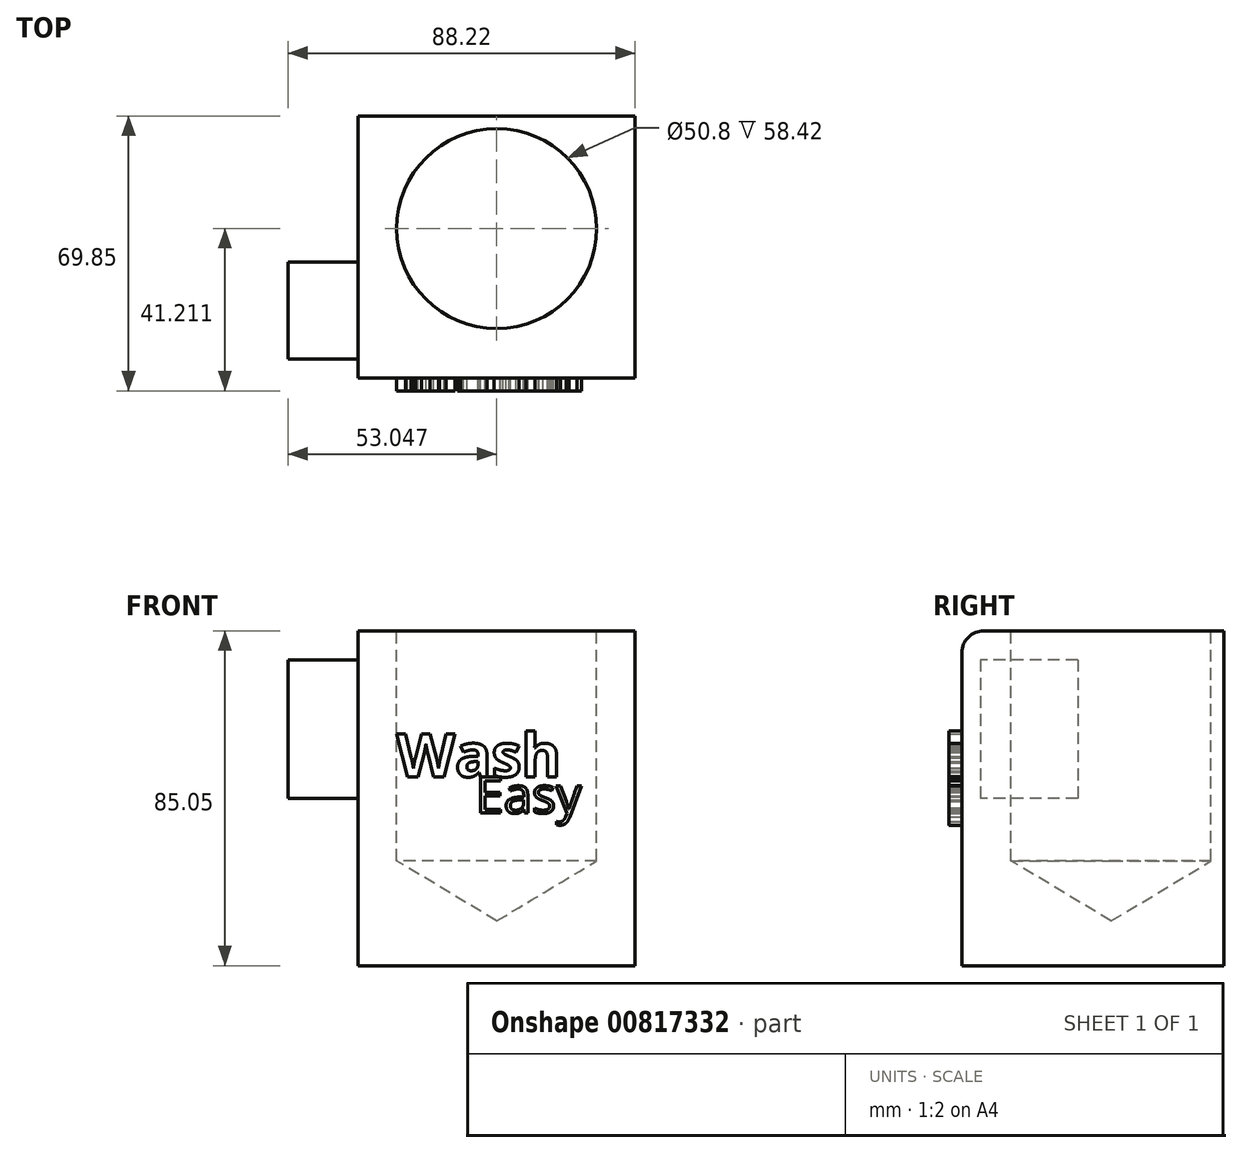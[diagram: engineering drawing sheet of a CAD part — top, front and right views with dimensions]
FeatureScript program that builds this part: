
annotation { "Feature Type Name" : "Feature", "Feature Type Description" : "" }
export const myFeature = defineFeature(function(context is Context, id is Id, definition is map)
    precondition{}
    {
        {
            var Q0;
            Q0=qCreatedBy(makeId("Front.planeOp"),FACE);
            var sketch = newSketch(context, id + "F0", { "sketchPlane" : qUnion([Q0])});
            skLineSegment(sketch, "E0.bottom", {"start": v(-26.72, 37.06) * mm, "end": v(43.72, 37.06) * mm});
            skLineSegment(sketch, "E0.top", {"start": v(-26.72, -47.99) * mm, "end": v(43.72, -47.99) * mm});
            skLineSegment(sketch, "E0.left", {"start": v(-26.72, 37.06) * mm, "end": v(-26.72, -47.99) * mm});
            skLineSegment(sketch, "E0.right", {"start": v(43.72, 37.06) * mm, "end": v(43.72, -47.99) * mm});
            skSolve(sketch);
        }
        {
            var Q0;
            Q0 = qSketchRegion(id + "F0", true);
            extrude(context, id + "F1", {"entities" : qUnion([Q0]), "depth" : 66.55 * mm, "offsetDistance" : 25.4 * mm});
        }
        {
            var Q0;
            Q0=makeQuery(id+"F1.opExtrude","SWEPT_FACE",FACE,{"disambiguationData":[OSD([sQuery(id+"F0.wireOp",EDGE,"E0.left")])]});
            var sketch = newSketch(context, id + "F2", { "sketchPlane" : qUnion([Q0])});
            skLineSegment(sketch, "E1.bottom", {"start": v(37.13, 29.71) * mm, "end": v(61.8, 29.71) * mm});
            skLineSegment(sketch, "E1.top", {"start": v(37.13, -5.46) * mm, "end": v(61.8, -5.46) * mm});
            skLineSegment(sketch, "E1.left", {"start": v(37.13, 29.71) * mm, "end": v(37.13, -5.46) * mm});
            skLineSegment(sketch, "E1.right", {"start": v(61.8, 29.71) * mm, "end": v(61.8, -5.46) * mm});
            skSolve(sketch);
        }
        {
            var Q0;
            Q0 = qSketchRegion(id + "F2", true);
            extrude(context, id + "F3", {"entities" : qUnion([Q0]), "operationType" : NewBodyOperationType.ADD, "depth" : 17.78 * mm, "offsetDistance" : 25.4 * mm});
        }
        {
            var Q0;
            Q0=makeQuery(id+"F1.opExtrude","SWEPT_FACE",FACE,{"disambiguationData":[OSD([sQuery(id+"F0.wireOp",EDGE,"E0.bottom")])]});
            var sketch = newSketch(context, id + "F4", { "sketchPlane" : qUnion([Q0])});
            skPoint(sketch, "E2", {"position": v(8.55, -28.64) * mm});
            skSolve(sketch);
        }
        {
            var Q0;
            Q0=sQuery(id+"F4.wireOp",VERTEX,"E2");
            var Q1;
            Q1=makeQuery(id+"F1.opExtrude","SWEPT_BODY",BODY,{"disambiguationData":[OSD([sQuery(id+"F0.wireOp",EDGE,"E0.bottom"),sQuery(id+"F0.wireOp",EDGE,"E0.top"),sQuery(id+"F0.wireOp",EDGE,"E0.left"),sQuery(id+"F0.wireOp",EDGE,"E0.right")])]});
            hole(context, id + "F5", {"style" : HoleStyle.SIMPLE, "endStyle" : HoleEndStyle.BLIND, "holeDiameter" : 50.8 * mm, "majorDiameter" : 6.35 * mm, "holeDepth" : 58.42 * mm, "isTappedThrough" : true, "tappedDepth" : 12.7 * mm, "tapClearance" : 3, "startFromSketch" : true, "locations" : qUnion([Q0]), "scope" : qUnion([Q1])});
        }
        {
            var Q0;
            Q0=makeQuery(id+"F1.opExtrude","CAP_EDGE",EDGE,{"disambiguationData":[OSD([sQuery(id+"F0.wireOp",EDGE,"E0.bottom")])],"isStart":false});
            fillet(context, id + "F6", {"entities" : qUnion([Q0]), "radius" : 5.52 * mm, "tangentPropagation" : true, "allowEdgeOverflow" : false});
        }
        {
            var Q0;
            Q0=makeQuery(id+"F1.opExtrude","CAP_FACE",FACE,{"disambiguationData":[OSD([sQuery(id+"F0.wireOp",EDGE,"E0.bottom"),sQuery(id+"F0.wireOp",EDGE,"E0.top"),sQuery(id+"F0.wireOp",EDGE,"E0.left"),sQuery(id+"F0.wireOp",EDGE,"E0.right")])],"isStart":false});
            var sketch = newSketch(context, id + "F7", { "sketchPlane" : qUnion([Q0])});
            skText(sketch, "E3", { "text": "Wash", "fontName": "OpenSans-Bold.ttf"});
            skText(sketch, "E4", { "text": "Easy", "fontName": "OpenSans-Regular.ttf"});
            const initialGuessF7  = {"E3": [-0.01684, 0, 1, 0, 0.01103], "E4": [0.00321, -0.00924, 1, 0, 0.00924]};
            skSetInitialGuess(sketch, initialGuessF7);
            skSolve(sketch);
        }
        {
            var Q0;
            Q0 = qSketchRegion(id + "F7", true);
            extrude(context, id + "F8", {"entities" : qUnion([Q0]), "operationType" : NewBodyOperationType.ADD, "depth" : 3.3 * mm, "offsetDistance" : 25.4 * mm});
        }
    });
